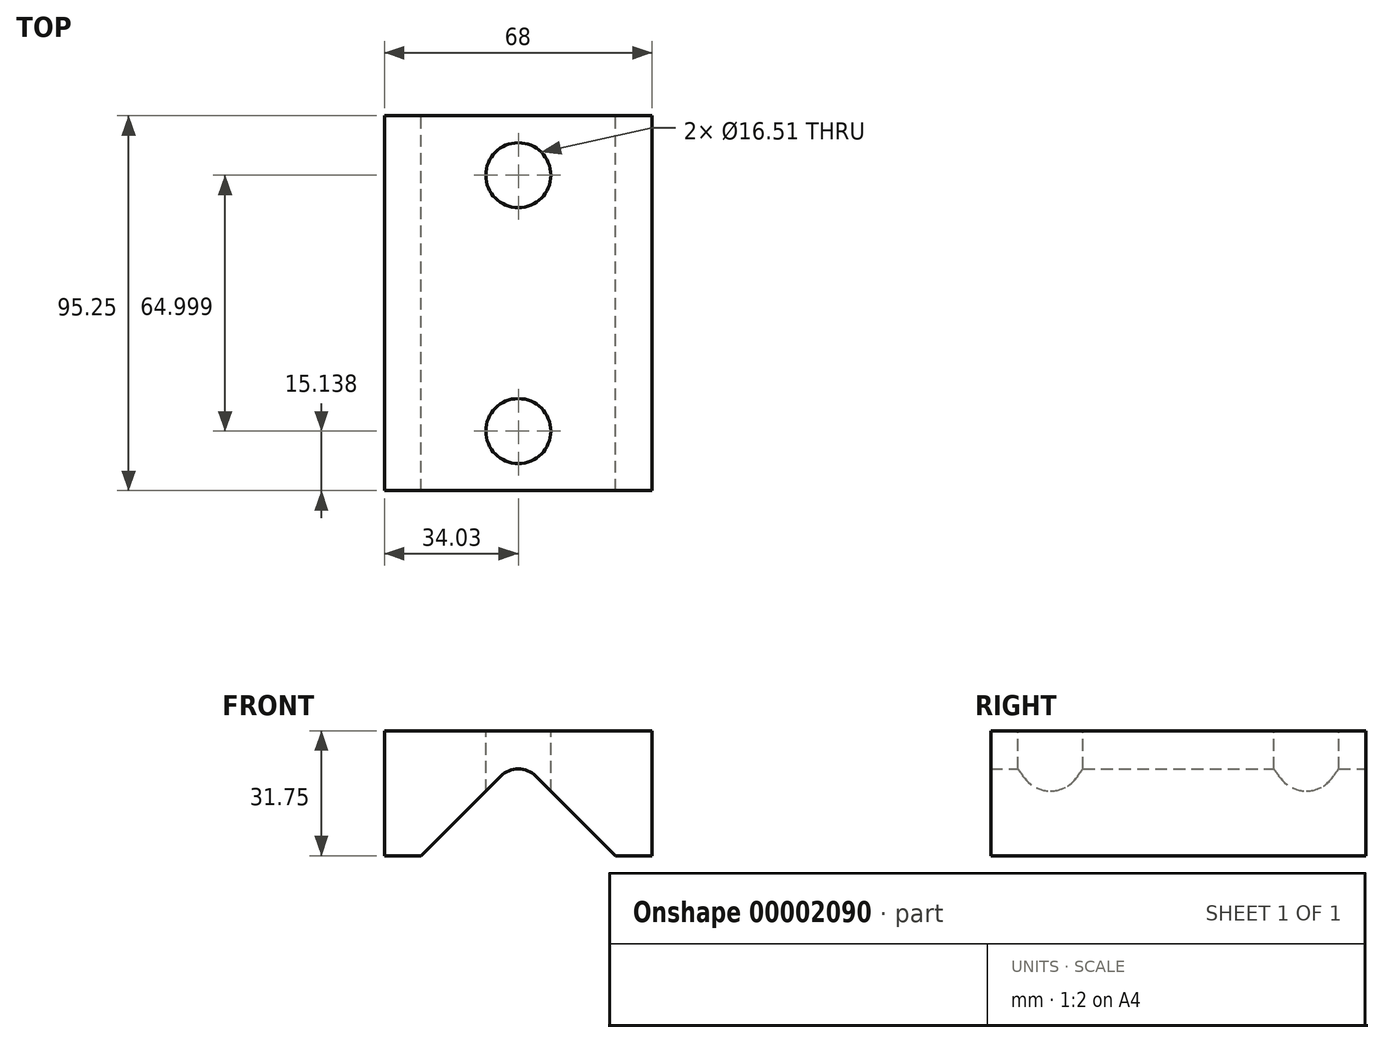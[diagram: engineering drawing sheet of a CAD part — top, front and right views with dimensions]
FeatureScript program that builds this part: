
annotation { "Feature Type Name" : "Feature", "Feature Type Description" : "" }
export const myFeature = defineFeature(function(context is Context, id is Id, definition is map)
    precondition{}
    {
        {
            var Q0;
            Q0=qCreatedBy(makeId("Front.planeOp"),FACE);
            var sketch = newSketch(context, id + "F0", { "sketchPlane" : qUnion([Q0])});
            skCircle(sketch, "E0", {"center": v(0, 0) * mm, "radius": 17.46 * mm});
            skLineSegment(sketch, "E1", {"start": v(-34.03, 0) * mm, "end": v(-34.03, 31.75) * mm});
            skLineSegment(sketch, "E2", {"start": v(-34.03, 31.75) * mm, "end": v(33.97, 31.75) * mm});
            skLineSegment(sketch, "E3", {"start": v(33.97, 31.75) * mm, "end": v(33.97, 0) * mm});
            skLineSegment(sketch, "E4", {"start": v(33.97, 0) * mm, "end": v(17.46, 0) * mm});
            skLineSegment(sketch, "E5", {"start": v(-34.03, 0) * mm, "end": v(-17.46, 0) * mm});
            skLineSegment(sketch, "E6", {"start": v(-4.5, 20.2) * mm, "end": v(-24.7, 0) * mm});
            skLineSegment(sketch, "E7", {"start": v(4.5, 20.2) * mm, "end": v(24.7, 0) * mm});
            skPoint(sketch, "E8.visualSharp", {"position": v(0, 24.7) * mm});
            skArc(sketch, "E8.filletArc", {"start": v(4.5, 20.2) * mm, "mid": v(0, 22.07) * mm, "end": v(-4.5, 20.2) * mm});
            skSolve(sketch);
        }
        {
            var Q0;
            {var subQ10=sQuery(id+"F0.wireOp",EDGE,"E1");Q0=makeQuery(id+"F0.imprint","IMPRINT",FACE,{"disambiguationData":[TD([[makeQuery(id+"F0.imprint","IMPRINT",EDGE,{"derivedFrom":subQ10}),-1.0]])]});}
            extrude(context, id + "F1", {"entities" : qUnion([Q0]), "depth" : 95.25 * mm});
        }
        {
            var Q0;
            Q0=makeQuery(id+"F1.opExtrude","SWEPT_FACE",FACE,{"disambiguationData":[OSD([sQuery(id+"F0.wireOp",EDGE,"E2")])]});
            var sketch = newSketch(context, id + "F2", { "sketchPlane" : qUnion([Q0])});
            skLineSegment(sketch, "E9", {"start": v(0, 0) * mm, "end": v(0, -95.25) * mm, "construction": true});
            skCircle(sketch, "E10", {"center": v(0, -15.11) * mm, "radius": 8.26 * mm});
            skCircle(sketch, "E11", {"center": v(0, -80.11) * mm, "radius": 8.26 * mm});
            skSolve(sketch);
        }
        {
            var Q0;
            Q0=makeQuery(id+"F2.imprint","IMPRINT",FACE,{"disambiguationData":[TD([[makeQuery(id+"F2.imprint","IMPRINT",EDGE,{"derivedFrom":sQuery(id+"F2.wireOp",EDGE,"E10")}),1.0]])]});
            var Q1;
            Q1=makeQuery(id+"F2.imprint","IMPRINT",FACE,{"disambiguationData":[TD([[makeQuery(id+"F2.imprint","IMPRINT",EDGE,{"derivedFrom":sQuery(id+"F2.wireOp",EDGE,"E11")}),1.0]])]});
            extrude(context, id + "F3", {"entities" : qUnion([Q0, Q1]), "operationType" : NewBodyOperationType.REMOVE, "endBound" : BoundingType.THROUGH_ALL, "oppositeDirection" : true, "depth" : 25.4 * mm});
        }
    });
